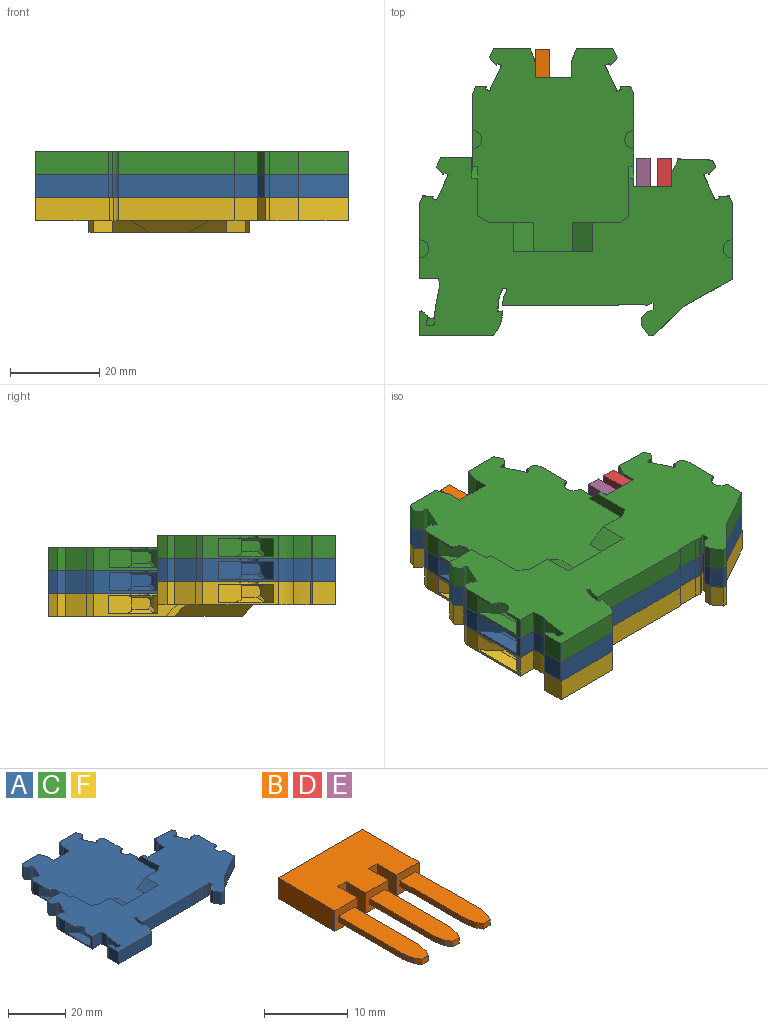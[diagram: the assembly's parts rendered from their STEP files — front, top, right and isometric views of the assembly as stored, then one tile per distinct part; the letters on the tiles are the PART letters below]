
ASSEMBLY  parts=6 mates=5
PART A: 246 faces, bbox 69.9x64.4x7.7 mm
  f0: plane 69.9x39.9mm, normal (0,0,-1), area 1802.7mm2, adj f2,f3,f4,f5,f6,f8,f9,f10
  f1: plane 45.58x36.1mm, normal (0,0,1), area 1276.1mm2, adj f52,f53,f54,f55,f56,f74,f75,f76
  f2: plane 5.15x1.16mm, normal (-0.17,-0.99,0), area 6.1mm2, adj f0,f4,f7,f244
  f3: plane 5.15x1.46mm, normal (-1,0,0), area 7.5mm2, adj f0,f7,f104,f242
  f4: plane 5.15x5.11mm, normal (0,-1,0), area 26.3mm2, adj f0,f2,f7,f9
  f5: cylinder r=0.5mm len=5.15mm, axis (0,0,1), area 8.1mm2, adj f0,f6,f7,f198
  f6: cylinder r=7.3mm len=5.15mm, axis (0,0,1), area 16.8mm2, adj f0,f5,f7,f8
  f7: plane 69.9x39.9mm, normal (0,0,1), area 1617.6mm2, adj f2,f3,f4,f5,f6,f8,f9,f10
  f8: plane 25.99x5.15mm, normal (0,-1,0), area 133.9mm2, adj f0,f6,f7,f9
  f9: plane 5.15x0.2mm, normal (1,0,0), area 1mm2, adj f0,f4,f7,f8
  f10: plane 5.15x1.35mm, normal (-0.71,0.71,0), area 9.8mm2, adj f0,f7,f11,f243
  f11: plane 5.15x1.65mm, normal (-1,0,0), area 8.5mm2, adj f0,f7,f10,f12
  f12: plane 5.15x2.4mm, normal (-0.82,-0.57,0), area 15.1mm2, adj f0,f7,f11,f13
  f13: plane 5.15x1.07mm, normal (0,-1,0), area 5.5mm2, adj f0,f7,f12,f241
  f14: plane 17.05x5.15mm, normal (1,0,0), area 35.9mm2, adj f0,f7,f15,f19,f20,f21,f25,f30
  f15: plane 5.15x1.54mm, normal (0.91,0.42,0), area 8.7mm2, adj f0,f7,f14,f16
  f16: plane 5.15x2.3mm, normal (-0.02,1,0), area 11.8mm2, adj f0,f7,f15,f17
  f17: plane 5.15x0.48mm, normal (-0.91,-0.42,0), area 2.7mm2, adj f0,f7,f16,f18
  f18: plane 5.15x0.97mm, normal (-0.42,0.91,0), area 5.5mm2, adj f0,f7,f17,f240
  f19: plane 0.55x0.52mm, normal (0.26,0.97,0), area 0.3mm2, adj f7,f14,f20,f38
  f20: plane 12.26x3.55mm, normal (0,0,-1), area 26mm2, adj f14,f19,f21,f22,f25,f35,f36,f37
  f21: plane 5.11x4.29mm, normal (0.77,-0.64,0), area 26.4mm2, adj f14,f20,f22,f30,f31,f33
  f22: plane 5.98x1.1mm, normal (0.34,0,-0.94), area 5.8mm2, adj f20,f21,f24,f25,f26,f33
  f23: plane 4.26x2.6mm, normal (1,0,0), area 10.6mm2, adj f24,f27,f28,f29,f32,f33
  f24: plane 8.15x4.07mm, normal (0,0,-1), area 29.1mm2, adj f22,f23,f26,f27,f33
  f25: plane 5.01x4.05mm, normal (0.5,0.87,0), area 20.5mm2, adj f14,f20,f22,f26,f28,f30,f34
  f26: plane 1.39x1.2mm, normal (0.71,0.5,-0.5), area 0.7mm2, adj f22,f24,f25,f27
  f27: plane 7.79x0.7mm, normal (0,0.71,-0.71), area 7.7mm2, adj f23,f24,f26,f28
  f28: plane 7.79x1.2mm, normal (0,1,0), area 9.3mm2, adj f23,f25,f27,f29
  f29: plane 7.79x0.7mm, normal (0,0.71,0.71), area 7.7mm2, adj f23,f28,f32,f34
  f30: plane 12.26x3.26mm, normal (0,0,1), area 30.5mm2, adj f14,f21,f25,f31,f34
  f31: plane 6.28x1.82mm, normal (0.5,0,0.87), area 9.8mm2, adj f21,f30,f32,f33,f34
  f32: plane 7.73x3.56mm, normal (0,0,1), area 27.5mm2, adj f23,f29,f31,f33
  f33: plane 8.51x3.19mm, normal (0,-1,0), area 22.3mm2, adj f21,f22,f23,f24,f31,f32
  f34: plane 2.12x1.89mm, normal (0.71,0.53,0.47), area 1.8mm2, adj f25,f29,f30,f31
  f35: plane 0.55x0.52mm, normal (0.26,-0.97,0), area 0.3mm2, adj f7,f14,f20,f36
  f36: cylinder r=2mm len=1.93mm, axis (0,0,1), area 1.4mm2, adj f7,f20,f35,f37
  f37: plane 0.55x0.03mm, normal (1,0,0), area 0mm2, adj f7,f20,f36,f38
  f38: cylinder r=2mm len=1.93mm, axis (0,0,1), area 1.4mm2, adj f7,f19,f20,f37
  f39: plane 11.18x6.27mm, normal (0.49,-0.87,0), area 66mm2, adj f0,f7,f14,f241
  f40: plane 5.15x0.97mm, normal (0.42,-0.91,0), area 5.5mm2, adj f0,f7,f41,f240
  f41: plane 5.15x0.48mm, normal (-0.91,-0.42,0), area 2.7mm2, adj f0,f7,f40,f239
  f42: plane 5.15x1.56mm, normal (0.91,0.42,0), area 8.9mm2, adj f0,f7,f229,f239
  f43: plane 8.45x2.58mm, normal (0,-0.71,-0.71), area 22.7mm2, adj f0,f44,f45,f227
  f44: plane 43.48x36mm, normal (0,0,-1), area 976.7mm2, adj f43,f45,f46,f47,f48,f49,f50,f51
  f45: plane 17.75x4.46mm, normal (0.5,0,-0.87), area 78.2mm2, adj f0,f43,f44,f48
  f46: plane 8.45x2.58mm, normal (0,-0.71,-0.71), area 22.7mm2, adj f0,f44,f47,f51
  f47: plane 17.75x4.46mm, normal (-0.5,0,-0.87), area 78.2mm2, adj f0,f44,f46,f48
  f48: plane 17.67x2.58mm, normal (0,-0.71,-0.71), area 48.1mm2, adj f0,f44,f45,f47
  f49: plane 4.08x2.58mm, normal (0.18,-0.98,0), area 10.7mm2, adj f0,f44,f50,f51
  f50: plane 3.51x2.58mm, normal (1,0,0), area 5.7mm2, adj f0,f44,f49,f57
  f51: plane 6.24x2.58mm, normal (-1,0,0), area 12.8mm2, adj f0,f44,f46,f49
  f52: plane 5.15x0.48mm, normal (0.91,-0.42,0), area 2.7mm2, adj f1,f44,f53,f54
  f53: plane 5.15x0.97mm, normal (0.42,0.91,0), area 5.5mm2, adj f1,f44,f52,f225
  f54: plane 5.15x2.3mm, normal (0.02,1,0), area 11.8mm2, adj f1,f44,f52,f55
  f55: plane 5.15x1.54mm, normal (-0.91,0.42,0), area 8.7mm2, adj f1,f44,f54,f56
  f56: plane 18.71x5.15mm, normal (-1,0,0), area 34.5mm2, adj f0,f1,f44,f55,f57,f58,f59,f61
  f57: plane 2.58x2.58mm, normal (0,-0.71,-0.71), area 4mm2, adj f0,f44,f50,f56
  f58: plane 10.82x3.55mm, normal (0,0,-1), area 23.4mm2, adj f56,f59,f62,f72,f74,f75,f76,f77
  f59: plane 4.05x3.9mm, normal (-0.18,0.98,0), area 15.7mm2, adj f56,f58,f60,f61,f71,f72,f73,f105
  f60: plane 1.46x1.25mm, normal (-0.71,0.5,-0.5), area 0.8mm2, adj f59,f64,f65,f71,f72
  f61: plane 10.82x3.26mm, normal (0,0,1), area 28mm2, adj f56,f59,f62,f69,f73
  f62: plane 5.11x4.29mm, normal (-0.77,-0.64,0), area 26.4mm2, adj f56,f58,f61,f69,f70,f72
  f63: plane 4.26x2.6mm, normal (-1,0,0), area 10.6mm2, adj f64,f65,f66,f67,f68,f70
  f64: plane 8.15x4.16mm, normal (0,0,-1), area 29.2mm2, adj f60,f63,f65,f70,f72
  f65: plane 7.73x0.7mm, normal (0,0.71,-0.71), area 7.6mm2, adj f60,f63,f64,f66
  f66: plane 7.73x1.2mm, normal (0,1,0), area 9.3mm2, adj f63,f65,f67,f71
  f67: plane 7.73x0.7mm, normal (0,0.71,0.71), area 7.6mm2, adj f63,f66,f68,f73
  f68: plane 7.73x3.56mm, normal (0,0,1), area 27.5mm2, adj f63,f67,f69,f70
  f69: plane 6.31x1.82mm, normal (-0.5,0,0.87), area 9.8mm2, adj f61,f62,f68,f70,f73
  f70: plane 8.51x3.19mm, normal (0,-1,0), area 22.3mm2, adj f62,f63,f64,f68,f69,f72
  f71: plane 3.02x1.18mm, normal (-0.54,0.84,0), area 2.9mm2, adj f59,f60,f66,f73
  f72: plane 5.95x1.1mm, normal (-0.34,0,-0.94), area 5.8mm2, adj f58,f59,f60,f62,f64,f70
  f73: plane 1.85x1.75mm, normal (-0.71,0.5,0.5), area 1.7mm2, adj f59,f61,f67,f69,f71
  f74: plane 0.55x0.52mm, normal (-0.26,0.97,0), area 0.3mm2, adj f1,f58,f75,f213
  f75: cylinder r=2mm len=1.93mm, axis (0,0,-1), area 1.4mm2, adj f1,f58,f74,f76
  f76: plane 0.55x0.03mm, normal (-1,0,0), area 0mm2, adj f1,f58,f75,f77
  f77: cylinder r=2mm len=1.93mm, axis (0,0,-1), area 1.4mm2, adj f1,f58,f76,f78
  f78: plane 0.55x0.52mm, normal (-0.26,-0.97,0), area 0.3mm2, adj f1,f56,f58,f77
  f79: plane 5.15x0.97mm, normal (-0.42,-0.91,0), area 5.5mm2, adj f1,f44,f224,f225
  f80: plane 5.15x1.73mm, normal (-0.75,-0.66,0), area 11.8mm2, adj f1,f44,f81,f224
  f81: plane 5.15x2.18mm, normal (-0.91,0.42,0), area 12.4mm2, adj f1,f44,f80,f216
  f82: plane 5.15x3.3mm, normal (0.94,0.34,0), area 18.1mm2, adj f1,f44,f83,f216
  f83: plane 14.85x5.15mm, normal (1,0,0), area 63.4mm2, adj f1,f44,f82,f84,f86,f87,f88
  f84: plane 11.65x3.15mm, normal (0,0,-1), area 36.7mm2, adj f83,f85,f87,f88
  f85: plane 11.65x4.03mm, normal (-1,0,0), area 46.9mm2, adj f84,f86,f87,f88
  f86: plane 11.65x3.15mm, normal (0,0,1), area 36.7mm2, adj f83,f85,f87,f88
  f87: plane 4.03x3.15mm, normal (0,1,0), area 12.7mm2, adj f83,f84,f85,f86
  f88: plane 8x5.15mm, normal (0,1,0), area 15.8mm2, adj f1,f44,f83,f84,f85,f86,f89,f90
  f89: plane 11.65x3.15mm, normal (0,0,-1), area 36.7mm2, adj f88,f90,f91,f92
  f90: plane 14.85x5.15mm, normal (-1,0,0), area 63.4mm2, adj f1,f44,f88,f89,f92,f93,f215
  f91: plane 11.65x4.03mm, normal (1,0,0), area 46.9mm2, adj f88,f89,f92,f93
  f92: plane 4.03x3.15mm, normal (0,1,0), area 12.7mm2, adj f89,f90,f91,f93
  f93: plane 11.65x3.15mm, normal (0,0,1), area 36.7mm2, adj f88,f90,f91,f92
  f94: plane 8.06x5.15mm, normal (0,1,0), area 27mm2, adj f1,f44,f97,f98,f214,f215
  f95: plane 3.45x3.17mm, normal (0,1,0), area 5.5mm2, adj f96,f97,f98
  f96: plane 3.04x3.04mm, normal (-0.71,0,-0.71), area 4.3mm2, adj f95,f98,f99
  f97: plane 8.27x2.12mm, normal (0,0,-1), area 17.5mm2, adj f94,f95,f98
  f98: cylinder r=2.17mm len=9.27mm, axis (0,-1,0), area 96.1mm2, adj f94,f95,f96,f97,f99,f100,f101
  f99: plane 3.53x3.53mm, normal (0,1,0), area 3mm2, adj f96,f98,f100
  f100: plane 3.04x3.04mm, normal (0.71,0,0.71), area 4.3mm2, adj f98,f99,f101
  f101: plane 3.45x3.45mm, normal (0,1,0), area 5.9mm2, adj f98,f100
  f102: plane 5.15x0.48mm, normal (-0.91,-0.42,0), area 2.7mm2, adj f1,f44,f103,f226
  f103: plane 5.15x1.73mm, normal (0.75,-0.66,0), area 11.8mm2, adj f1,f44,f102,f214
  f104: plane 5.15x0.43mm, normal (0,-1,0), area 2.2mm2, adj f0,f3,f7,f245
  f105: plane 7.13x5.15mm, normal (0,1,0), area 21.8mm2, adj f0,f1,f7,f59,f108,f109,f113,f212
  f106: plane 3.45x3.17mm, normal (0,1,0), area 5.5mm2, adj f107,f108,f109
  f107: plane 3.04x3.04mm, normal (-0.71,0,-0.71), area 4.3mm2, adj f106,f109,f110
  f108: plane 8.27x2.12mm, normal (0,0,-1), area 17.5mm2, adj f105,f106,f109
  f109: cylinder r=2.17mm len=9.27mm, axis (0,-1,0), area 96.1mm2, adj f105,f106,f107,f108,f110,f111,f112
  f110: plane 3.53x3.53mm, normal (0,1,0), area 3mm2, adj f107,f109,f111
  f111: plane 3.04x3.04mm, normal (0.71,0,0.71), area 4.3mm2, adj f109,f110,f112
  f112: plane 3.45x3.45mm, normal (0,1,0), area 5.9mm2, adj f109,f111
  f113: plane 4.63x2.58mm, normal (1,0,0.05), area 8.6mm2, adj f1,f7,f105,f115
  f114: plane 10.93x2.58mm, normal (1,0,0), area 24.8mm2, adj f1,f7,f115,f163
  f115: plane 2.58x2.58mm, normal (0,0.71,0.71), area 4.6mm2, adj f1,f7,f113,f114
  f116: plane 10.43x2.58mm, normal (0,1,0), area 21.1mm2, adj f1,f7,f117,f162
  f117: plane 2.58x2.1mm, normal (-0.53,0.85,0), area 6.4mm2, adj f1,f7,f116,f158
  f118: plane 14.93x5.15mm, normal (-1,0,0), area 63.8mm2, adj f0,f7,f120,f121,f122,f123,f238
  f119: plane 11.65x4.03mm, normal (1,0,0), area 46.9mm2, adj f120,f121,f122,f123
  f120: plane 11.65x3.15mm, normal (0,0,-1), area 36.7mm2, adj f118,f119,f121,f123
  f121: plane 4.03x3.15mm, normal (0,1,0), area 12.7mm2, adj f118,f119,f120,f122
  f122: plane 11.65x3.15mm, normal (0,0,1), area 36.7mm2, adj f118,f119,f121,f123
  f123: plane 8.55x5.15mm, normal (0,1,0), area 18.7mm2, adj f0,f7,f118,f119,f120,f122,f124,f125
  f124: plane 11.65x4.03mm, normal (-1,0,0), area 46.9mm2, adj f123,f125,f126,f127
  f125: plane 11.65x3.15mm, normal (0,0,1), area 36.7mm2, adj f123,f124,f126,f128
  f126: plane 4.03x3.15mm, normal (0,1,0), area 12.7mm2, adj f124,f125,f127,f128
  f127: plane 11.65x3.15mm, normal (0,0,-1), area 36.7mm2, adj f123,f124,f126,f128
  f128: plane 11.65x4.03mm, normal (1,0,0), area 46.9mm2, adj f123,f125,f126,f127
  f129: plane 20.78x7.73mm, normal (1,0,0), area 60.4mm2, adj f0,f1,f7,f44,f123,f132,f133,f134
  f130: plane 0.55x0.03mm, normal (1,0,0), area 0mm2, adj f1,f131,f133,f146
  f131: cylinder r=2mm len=1.93mm, axis (0,0,1), area 1.4mm2, adj f1,f130,f132,f133
  f132: plane 0.55x0.52mm, normal (0.26,0.97,0), area 0.3mm2, adj f1,f129,f131,f133
  f133: plane 10.82x3.55mm, normal (0,0,-1), area 23.4mm2, adj f129,f130,f131,f132,f134,f135,f146,f147
  f134: plane 5.11x4.29mm, normal (0.77,-0.64,0), area 26.4mm2, adj f129,f133,f135,f139,f143,f148
  f135: plane 5.95x1.1mm, normal (0.34,0,-0.94), area 5.8mm2, adj f133,f134,f138,f139,f145,f150
  f136: plane 3.02x1.18mm, normal (0.54,0.84,0), area 2.9mm2, adj f137,f145,f149,f150
  f137: plane 7.73x1.2mm, normal (0,1,0), area 9.3mm2, adj f136,f140,f141,f144
  f138: plane 8.15x4.16mm, normal (0,0,-1), area 29.2mm2, adj f135,f139,f140,f144,f145
  f139: plane 8.51x3.19mm, normal (0,-1,0), area 22.3mm2, adj f134,f135,f138,f140,f142,f143
  f140: plane 4.26x2.6mm, normal (1,0,0), area 10.6mm2, adj f137,f138,f139,f141,f142,f144
  f141: plane 7.73x0.7mm, normal (0,0.71,0.71), area 7.6mm2, adj f137,f140,f142,f149
  f142: plane 7.73x3.56mm, normal (0,0,1), area 27.5mm2, adj f139,f140,f141,f143
  f143: plane 6.31x1.82mm, normal (0.5,0,0.87), area 9.8mm2, adj f134,f139,f142,f148,f149
  f144: plane 7.73x0.7mm, normal (0,0.71,-0.71), area 7.6mm2, adj f137,f138,f140,f145
  f145: plane 1.46x1.25mm, normal (0.71,0.5,-0.5), area 0.8mm2, adj f135,f136,f138,f144,f150
  f146: cylinder r=2mm len=1.93mm, axis (0,0,1), area 1.4mm2, adj f1,f130,f133,f147
  f147: plane 0.55x0.52mm, normal (0.26,-0.97,0), area 0.3mm2, adj f1,f129,f133,f146
  f148: plane 10.82x3.26mm, normal (0,0,1), area 28mm2, adj f129,f134,f143,f149,f150
  f149: plane 1.85x1.75mm, normal (0.71,0.5,0.5), area 1.7mm2, adj f136,f141,f143,f148,f150
  f150: plane 4.05x3.9mm, normal (0.18,0.98,0), area 15.7mm2, adj f129,f133,f135,f136,f145,f148,f149
  f151: plane 5.15x1.54mm, normal (0.91,0.42,0), area 8.7mm2, adj f1,f44,f129,f155
  f152: plane 5.15x0.97mm, normal (-0.42,0.91,0), area 5.5mm2, adj f1,f44,f153,f154
  f153: plane 5.15x0.48mm, normal (-0.91,-0.42,0), area 2.7mm2, adj f1,f44,f152,f155
  f154: plane 5.73x5.15mm, normal (0.91,0.42,0), area 32.6mm2, adj f1,f44,f152,f226
  f155: plane 5.15x2.3mm, normal (-0.02,1,0), area 11.8mm2, adj f1,f44,f151,f153
  f156: plane 3.51x2.58mm, normal (-1,0,0), area 5.7mm2, adj f0,f44,f157,f228
  f157: plane 2.58x2.58mm, normal (0,-0.71,-0.71), area 4mm2, adj f0,f44,f129,f156
  f158: plane 11.25x2.58mm, normal (-1,0,0), area 25.6mm2, adj f1,f7,f117,f159
  f159: plane 2.58x2.58mm, normal (0,0.71,0.71), area 4mm2, adj f1,f7,f129,f158
  f160: plane 6.5x4.46mm, normal (0.5,0,0.87), area 33.5mm2, adj f1,f7,f161,f164
  f161: plane 17.67x2.58mm, normal (0,1,0), area 34mm2, adj f1,f7,f160,f162
  f162: plane 6.5x4.46mm, normal (-0.5,0,0.87), area 33.5mm2, adj f1,f7,f116,f161
  f163: plane 2.61x2.58mm, normal (0.53,0.85,0), area 7.9mm2, adj f1,f7,f114,f164
  f164: plane 9.92x2.58mm, normal (0,1,0), area 19.8mm2, adj f1,f7,f160,f163
  f165: plane 5.15x1.73mm, normal (-0.75,-0.66,0), area 11.8mm2, adj f0,f7,f166,f212
  f166: plane 5.15x0.48mm, normal (0.91,-0.42,0), area 2.7mm2, adj f0,f7,f165,f167
  f167: plane 5.15x0.97mm, normal (-0.42,-0.91,0), area 5.5mm2, adj f0,f7,f166,f211
  f168: plane 5.15x2.3mm, normal (0.02,1,0), area 11.8mm2, adj f0,f7,f208,f210
  f169: plane 16.88x5.15mm, normal (-1,0,0), area 35mm2, adj f0,f7,f170,f172,f173,f174,f175,f176
  f170: plane 5.15x4.24mm, normal (0,-1,0), area 21.9mm2, adj f0,f7,f169,f171
  f171: cylinder r=7.5mm len=5.15mm, axis (0,0,1), area 17.4mm2, adj f0,f7,f170,f200
  f172: plane 0.55x0.52mm, normal (-0.26,-0.97,0), area 0.3mm2, adj f7,f169,f173,f191
  f173: plane 12.26x3.55mm, normal (0,0,-1), area 26mm2, adj f169,f172,f174,f176,f179,f188,f189,f190
  f174: plane 5.01x4.05mm, normal (-0.5,0.87,0), area 20.5mm2, adj f169,f173,f175,f179,f181,f182,f187
  f175: plane 12.26x3.26mm, normal (0,0,1), area 30.5mm2, adj f169,f174,f176,f182,f183
  f176: plane 5.11x4.29mm, normal (-0.77,-0.64,0), area 26.4mm2, adj f169,f173,f175,f179,f183,f186
  f177: plane 4.26x2.6mm, normal (-1,0,0), area 10.6mm2, adj f178,f180,f181,f184,f185,f186
  f178: plane 8.15x4.07mm, normal (0,0,-1), area 29.1mm2, adj f177,f179,f180,f186,f187
  f179: plane 5.98x1.1mm, normal (-0.34,0,-0.94), area 5.8mm2, adj f173,f174,f176,f178,f186,f187
  f180: plane 7.79x0.7mm, normal (0,0.71,-0.71), area 7.7mm2, adj f177,f178,f181,f187
  f181: plane 7.79x1.2mm, normal (0,1,0), area 9.3mm2, adj f174,f177,f180,f185
  f182: plane 2.12x1.89mm, normal (-0.71,0.53,0.47), area 1.8mm2, adj f174,f175,f183,f185
  f183: plane 6.28x1.82mm, normal (-0.5,0,0.87), area 9.8mm2, adj f175,f176,f182,f184,f186
  f184: plane 7.73x3.56mm, normal (0,0,1), area 27.5mm2, adj f177,f183,f185,f186
  f185: plane 7.79x0.7mm, normal (0,0.71,0.71), area 7.7mm2, adj f177,f181,f182,f184
  f186: plane 8.51x3.19mm, normal (0,-1,0), area 22.3mm2, adj f176,f177,f178,f179,f183,f184
  f187: plane 1.39x1.2mm, normal (-0.71,0.5,-0.5), area 0.7mm2, adj f174,f178,f179,f180
  f188: plane 0.55x0.52mm, normal (-0.26,0.97,0), area 0.3mm2, adj f7,f169,f173,f189
  f189: cylinder r=2mm len=1.93mm, axis (0,0,-1), area 1.4mm2, adj f7,f173,f188,f190
  f190: plane 0.55x0.03mm, normal (-1,0,0), area 0mm2, adj f7,f173,f189,f191
  f191: cylinder r=2mm len=1.93mm, axis (0,0,-1), area 1.4mm2, adj f7,f172,f173,f190
  f192: plane 4.55x1.71mm, normal (0,1,0), area 7.8mm2, adj f7,f200,f206,f207
  f193: plane 16.39x5.15mm, normal (0,-1,0), area 84.4mm2, adj f0,f7,f194,f203
  f194: cylinder r=9.5mm len=5.15mm, axis (0,0,1), area 7.8mm2, adj f0,f7,f193,f195
  f195: cylinder r=7mm len=5.15mm, axis (0,0,1), area 20.7mm2, adj f0,f7,f194,f196
  f196: plane 5.15x0.56mm, normal (1,0,0), area 2.9mm2, adj f0,f7,f195,f197
  f197: plane 5.15x0.9mm, normal (-0.09,1,0), area 4.7mm2, adj f0,f7,f196,f199
  f198: cylinder r=8.3mm len=5.15mm, axis (0,0,1), area 20.8mm2, adj f0,f5,f7,f199
  f199: plane 5.15x1.08mm, normal (1,0,0), area 5.6mm2, adj f0,f7,f197,f198
  f200: cylinder r=32.1mm len=7.14mm, axis (0,0,1), area 35.9mm2, adj f0,f7,f171,f192,f204,f206
  f201: plane 5.15x1.37mm, normal (0.71,0.71,0), area 6.7mm2, adj f0,f7,f202,f204,f205,f206
  f202: cylinder r=0.4mm len=5.15mm, axis (0,0,1), area 4.9mm2, adj f0,f7,f201,f203
  f203: plane 5.16x5.15mm, normal (-1,0,0), area 26.6mm2, adj f0,f7,f193,f202
  f204: cylinder r=0.75mm len=1.28mm, axis (0,0,1), area 1mm2, adj f0,f200,f201,f206
  f205: cylinder r=0.9mm len=4.55mm, axis (0,0,1), area 6.7mm2, adj f7,f201,f206,f207
  f206: plane 2.24x1.83mm, normal (0,0,1), area 2.7mm2, adj f192,f200,f201,f204,f205,f207
  f207: plane 4.55x0.93mm, normal (1,0,0), area 4.2mm2, adj f7,f192,f205,f206
  f208: plane 5.15x1.54mm, normal (-0.91,0.42,0), area 8.7mm2, adj f0,f7,f168,f169
  f209: plane 5.15x0.97mm, normal (0.42,0.91,0), area 5.5mm2, adj f0,f7,f210,f211
  f210: plane 5.15x0.48mm, normal (0.91,-0.42,0), area 2.7mm2, adj f0,f7,f168,f209
  f211: plane 5.73x5.15mm, normal (-0.91,0.42,0), area 32.6mm2, adj f0,f7,f167,f209
  f212: plane 5.15x2.18mm, normal (-0.91,0.42,0), area 12.4mm2, adj f0,f7,f105,f165
  f213: plane 1.91x0.55mm, normal (-1,0,0), area 1.1mm2, adj f1,f58,f74,f105
  f214: plane 5.15x2.18mm, normal (0.91,0.42,0), area 12.4mm2, adj f1,f44,f94,f103
  f215: plane 5.15x3.3mm, normal (-0.94,0.34,0), area 18.1mm2, adj f1,f44,f90,f94
  f216: plane 8.06x5.15mm, normal (0,1,0), area 27mm2, adj f1,f44,f81,f82,f219,f220
  f217: plane 3.45x3.17mm, normal (0,1,0), area 5.5mm2, adj f218,f219,f220
  f218: plane 3.04x3.04mm, normal (-0.71,0,-0.71), area 4.3mm2, adj f217,f220,f221
  f219: plane 8.27x2.12mm, normal (0,0,-1), area 17.5mm2, adj f216,f217,f220
  f220: cylinder r=2.17mm len=9.27mm, axis (0,-1,0), area 96.1mm2, adj f216,f217,f218,f219,f221,f222,f223
  f221: plane 3.53x3.53mm, normal (0,1,0), area 3mm2, adj f218,f220,f222
  f222: plane 3.04x3.04mm, normal (0.71,0,0.71), area 4.3mm2, adj f220,f221,f223
  f223: plane 3.45x3.45mm, normal (0,1,0), area 5.9mm2, adj f220,f222
  f224: plane 5.15x0.48mm, normal (0.91,-0.42,0), area 2.7mm2, adj f1,f44,f79,f80
  f225: plane 5.73x5.15mm, normal (-0.91,0.42,0), area 32.6mm2, adj f1,f44,f53,f79
  f226: plane 5.15x0.97mm, normal (0.42,-0.91,0), area 5.5mm2, adj f1,f44,f102,f154
  f227: plane 6.24x2.58mm, normal (1,0,0), area 12.8mm2, adj f0,f43,f44,f228
  f228: plane 4.08x2.58mm, normal (-0.18,-0.98,0), area 10.7mm2, adj f0,f44,f156,f227
  f229: plane 7.82x5.15mm, normal (0.03,1,0), area 25.8mm2, adj f0,f7,f42,f232,f233,f237
  f230: plane 3.45x3.17mm, normal (0,1,0), area 5.5mm2, adj f231,f232,f233
  f231: plane 3.04x3.04mm, normal (-0.71,0,-0.71), area 4.3mm2, adj f230,f233,f234
  f232: plane 7.84x2.12mm, normal (0,0,-1), area 16.5mm2, adj f229,f230,f233
  f233: cylinder r=2.17mm len=8.88mm, axis (0,-1,0), area 90.8mm2, adj f229,f230,f231,f232,f234,f235,f236
  f234: plane 3.53x3.53mm, normal (0,1,0), area 3mm2, adj f231,f233,f235
  f235: plane 3.04x3.04mm, normal (0.71,0,0.71), area 4.3mm2, adj f233,f234,f236
  f236: plane 3.45x3.45mm, normal (0,1,0), area 5.9mm2, adj f233,f235
  f237: plane 5.15x0.65mm, normal (-1,0,0), area 3.3mm2, adj f0,f7,f229,f238
  f238: plane 5.15x2.23mm, normal (-0.88,0.47,0), area 13mm2, adj f0,f7,f118,f237
  f239: plane 5.15x1.73mm, normal (0.75,-0.66,0), area 11.8mm2, adj f0,f7,f41,f42
  f240: plane 5.73x5.15mm, normal (0.91,0.42,0), area 32.6mm2, adj f0,f7,f18,f40
  f241: plane 6.41x6.4mm, normal (0.71,-0.71,0), area 46.6mm2, adj f0,f7,f13,f39
  f242: plane 5.15x0.32mm, normal (-0.5,0.87,0), area 1.9mm2, adj f0,f3,f7,f243
  f243: plane 5.15x0.97mm, normal (-0.26,0.97,0), area 5.2mm2, adj f0,f7,f10,f242
  f244: plane 5.15x0.2mm, normal (0,-1,0), area 1mm2, adj f0,f2,f7,f245
  f245: plane 5.15x0.79mm, normal (0.51,-0.86,0), area 4.7mm2, adj f0,f7,f104,f244
PART B: 41 faces, bbox 14.2x22.9x3 mm
  f0: plane 3.8x3mm, normal (0,-1,0), area 9.3mm2, adj f1,f5,f7,f9,f10,f11,f39,f40
  f1: plane 3.31x3mm, normal (-1,0,0), area 9.9mm2, adj f0,f2,f39,f40
  f2: plane 3x1.4mm, normal (0,-1,0), area 4.2mm2, adj f1,f21,f39,f40
  f3: plane 0.83x0.8mm, normal (0.86,-0.5,0), area 0.8mm2, adj f4,f5,f9,f12
  f4: plane 1.61x0.8mm, normal (0.98,-0.19,0), area 1.3mm2, adj f3,f5,f9,f10
  f5: plane 13.31x2.68mm, normal (0,0,-1), area 34.2mm2, adj f0,f3,f4,f7,f8,f10,f12,f13
  f6: plane 14.2x3mm, normal (0,1,0), area 42.6mm2, adj f11,f35,f39,f40
  f7: plane 10.87x0.8mm, normal (-1,0,0), area 8.7mm2, adj f0,f5,f8,f9
  f8: plane 1.61x0.8mm, normal (-0.98,-0.19,0), area 1.3mm2, adj f5,f7,f9,f13
  f9: plane 13.31x2.68mm, normal (0,0,1), area 34.2mm2, adj f0,f3,f4,f7,f8,f10,f12,f13
  f10: plane 10.87x0.8mm, normal (1,0,0), area 8.7mm2, adj f0,f4,f5,f9
  f11: plane 9.61x3mm, normal (1,0,0), area 28.8mm2, adj f0,f6,f39,f40
  f12: plane 1.09x0.8mm, normal (0,-1,0), area 0.9mm2, adj f3,f5,f9,f13
  f13: plane 0.83x0.8mm, normal (-0.86,-0.5,0), area 0.8mm2, adj f5,f8,f9,f12
  f14: plane 1.09x0.8mm, normal (0,-1,0), area 0.9mm2, adj f17,f31,f34,f38
  f15: plane 10.87x0.8mm, normal (-1,0,0), area 8.7mm2, adj f31,f33,f36,f38
  f16: plane 10.87x0.8mm, normal (1,0,0), area 8.7mm2, adj f18,f31,f36,f38
  f17: plane 0.83x0.8mm, normal (0.86,-0.5,0), area 0.8mm2, adj f14,f18,f31,f38
  f18: plane 1.61x0.8mm, normal (0.98,-0.19,0), area 1.3mm2, adj f16,f17,f31,f38
  f19: plane 3.31x3mm, normal (-1,0,0), area 9.9mm2, adj f20,f32,f39,f40
  f20: plane 3.8x3mm, normal (0,-1,0), area 9.3mm2, adj f19,f21,f22,f23,f24,f25,f39,f40
  f21: plane 3.31x3mm, normal (1,0,0), area 9.9mm2, adj f2,f20,f39,f40
  f22: plane 13.31x2.68mm, normal (0,0,1), area 34.2mm2, adj f20,f23,f25,f26,f27,f28,f29,f30
  f23: plane 10.87x0.8mm, normal (1,0,0), area 8.7mm2, adj f20,f22,f24,f30
  f24: plane 13.31x2.68mm, normal (0,0,-1), area 34.2mm2, adj f20,f23,f25,f26,f27,f28,f29,f30
  f25: plane 10.87x0.8mm, normal (-1,0,0), area 8.7mm2, adj f20,f22,f24,f26
  f26: plane 1.61x0.8mm, normal (-0.98,-0.19,0), area 1.3mm2, adj f22,f24,f25,f27
  f27: plane 0.83x0.8mm, normal (-0.86,-0.5,0), area 0.8mm2, adj f22,f24,f26,f28
  f28: plane 1.09x0.8mm, normal (0,-1,0), area 0.9mm2, adj f22,f24,f27,f29
  f29: plane 0.83x0.8mm, normal (0.86,-0.5,0), area 0.8mm2, adj f22,f24,f28,f30
  f30: plane 1.61x0.8mm, normal (0.98,-0.19,0), area 1.3mm2, adj f22,f23,f24,f29
  f31: plane 13.31x2.68mm, normal (0,0,1), area 34.2mm2, adj f14,f15,f16,f17,f18,f33,f34,f36
  f32: plane 3x1.4mm, normal (0,-1,0), area 4.2mm2, adj f19,f37,f39,f40
  f33: plane 1.61x0.8mm, normal (-0.98,-0.19,0), area 1.3mm2, adj f15,f31,f34,f38
  f34: plane 0.83x0.8mm, normal (-0.86,-0.5,0), area 0.8mm2, adj f14,f31,f33,f38
  f35: plane 9.61x3mm, normal (-1,0,0), area 28.8mm2, adj f6,f36,f39,f40
  f36: plane 3.8x3mm, normal (0,-1,0), area 9.3mm2, adj f15,f16,f31,f35,f37,f38,f39,f40
  f37: plane 3.31x3mm, normal (1,0,0), area 9.9mm2, adj f32,f36,f39,f40
  f38: plane 13.31x2.68mm, normal (0,0,-1), area 34.2mm2, adj f14,f15,f16,f17,f18,f33,f34,f36
  f39: plane 14.2x9.61mm, normal (0,0,1), area 127.1mm2, adj f0,f1,f2,f6,f11,f19,f20,f21
  f40: plane 14.2x9.61mm, normal (0,0,-1), area 127.1mm2, adj f0,f1,f2,f6,f11,f19,f20,f21
PART C: same geometry as A
PART D: same geometry as B
PART E: same geometry as B
PART F: same geometry as A
PLACE A t=(-13.67,12.46,4.91)mm
PLACE B rot(axis=(0,1,0),90deg) t=(26.95,51.64,-7.25)mm
PLACE C t=(-13.66,12.47,10.05)mm
PLACE D rot(axis=(0,-1,0),90deg) t=(54.23,27.23,9.54)mm
PLACE E rot(axis=(0,1,0),90deg) t=(49.46,27.23,-4.7)mm
PLACE F t=(-13.61,12.49,-0.21)mm
MATE planar D.f32 <-> F.f123  axis (0,-1,0) through (54.23,30.53,-0.16)mm
MATE planar E.f2 <-> F.f123  axis (0,-1,0) through (49.46,30.53,-0.2)mm
MATE planar C.f39 <-> F.f39  axis (0.49,-0.87,0) through (63.75,6.65,10.05)mm
MATE planar F.f39 <-> A.f39  axis (0.49,-0.87,0) through (58.21,3.54,-2.79)mm
MATE planar B.f32 <-> A.f88  axis (0,-1,0) through (28.45,54.95,2.45)mm
